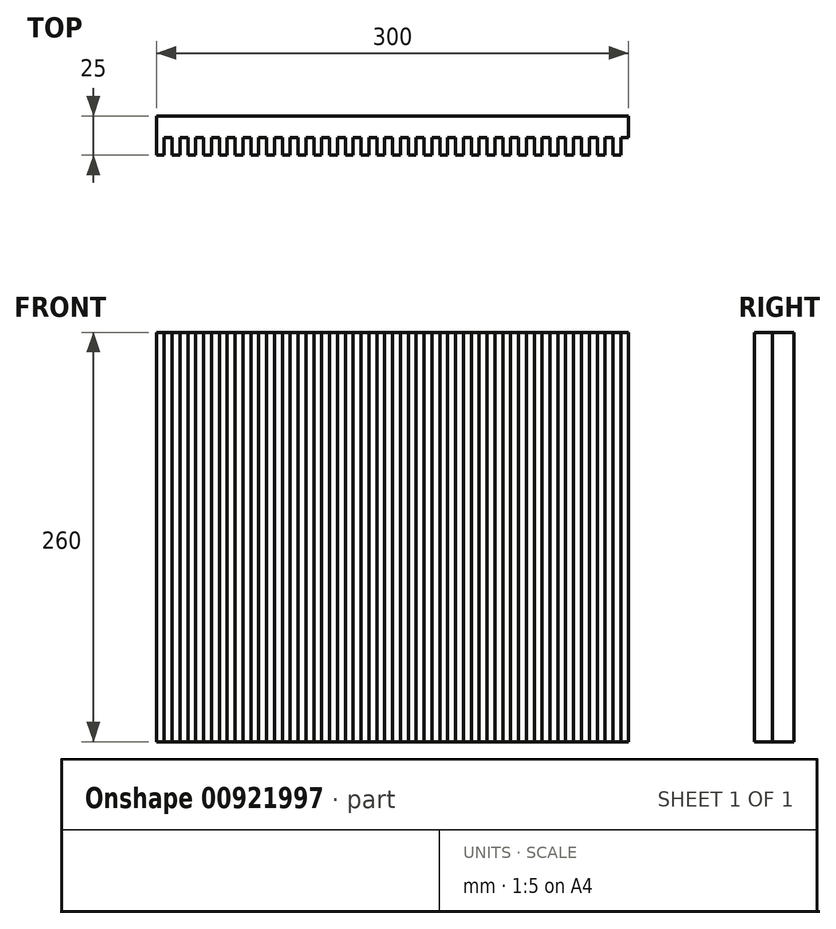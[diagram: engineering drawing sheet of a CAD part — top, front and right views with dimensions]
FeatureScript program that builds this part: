
annotation { "Feature Type Name" : "Feature", "Feature Type Description" : "" }
export const myFeature = defineFeature(function(context is Context, id is Id, definition is map)
    precondition{}
    {
        {
            var Q0;
            Q0=qCreatedBy(makeId("Front.planeOp"),FACE);
            var sketch = newSketch(context, id + "F0", { "sketchPlane" : qUnion([Q0])});
            skLineSegment(sketch, "E0.bottom", {"start": v(0, 0) * mm, "end": v(300, 0) * mm});
            skLineSegment(sketch, "E0.top", {"start": v(0, 260) * mm, "end": v(300, 260) * mm});
            skLineSegment(sketch, "E0.left", {"start": v(0, 0) * mm, "end": v(0, 260) * mm});
            skLineSegment(sketch, "E0.right", {"start": v(300, 0) * mm, "end": v(300, 260) * mm});
            skSolve(sketch);
        }
        {
            var Q0;
            Q0=makeQuery(id+"F0.imprint","IMPRINT",FACE,{"disambiguationData":[TD([[makeQuery(id+"F0.imprint","IMPRINT",EDGE,{"derivedFrom":sQuery(id+"F0.wireOp",EDGE,"E0.bottom")}),1.0]])]});
            extrude(context, id + "F1", {"entities" : qUnion([Q0]), "oppositeDirection" : true, "depth" : 25 * mm, "offsetDistance" : 25 * mm});
        }
        {
            var Q0;
            Q0=makeQuery(id+"F1.opExtrude","CAP_FACE",FACE,{"disambiguationData":[OSD([sQuery(id+"F0.wireOp",EDGE,"E0.bottom"),sQuery(id+"F0.wireOp",EDGE,"E0.top"),sQuery(id+"F0.wireOp",EDGE,"E0.left"),sQuery(id+"F0.wireOp",EDGE,"E0.right")])],"isStart":true});
            var sketch = newSketch(context, id + "F2", { "sketchPlane" : qUnion([Q0])});
            skLineSegment(sketch, "E1.bottom", {"start": v(5, 260) * mm, "end": v(10, 260) * mm});
            skLineSegment(sketch, "E1.top", {"start": v(5, 0) * mm, "end": v(10, 0) * mm});
            skLineSegment(sketch, "E1.left", {"start": v(5, 260) * mm, "end": v(5, 0) * mm});
            skLineSegment(sketch, "E1.right", {"start": v(10, 260) * mm, "end": v(10, 0) * mm});
            skLineSegment(sketch, "E2.1.0.0", {"start": v(15, 260) * mm, "end": v(15, 0) * mm});
            skLineSegment(sketch, "E2.1.0.1", {"start": v(20, 260) * mm, "end": v(20, 0) * mm});
            skLineSegment(sketch, "E2.1.0.2", {"start": v(15, 0) * mm, "end": v(20, 0) * mm});
            skLineSegment(sketch, "E2.1.0.3", {"start": v(15, 260) * mm, "end": v(20, 260) * mm});
            skLineSegment(sketch, "E2.2.0.0", {"start": v(25, 260) * mm, "end": v(25, 0) * mm});
            skLineSegment(sketch, "E2.2.0.1", {"start": v(30, 260) * mm, "end": v(30, 0) * mm});
            skLineSegment(sketch, "E2.2.0.2", {"start": v(25, 0) * mm, "end": v(30, 0) * mm});
            skLineSegment(sketch, "E2.2.0.3", {"start": v(25, 260) * mm, "end": v(30, 260) * mm});
            skLineSegment(sketch, "E2.3.0.0", {"start": v(35, 260) * mm, "end": v(35, 0) * mm});
            skLineSegment(sketch, "E2.3.0.1", {"start": v(40, 260) * mm, "end": v(40, 0) * mm});
            skLineSegment(sketch, "E2.3.0.2", {"start": v(35, 0) * mm, "end": v(40, 0) * mm});
            skLineSegment(sketch, "E2.3.0.3", {"start": v(35, 260) * mm, "end": v(40, 260) * mm});
            skLineSegment(sketch, "E2.4.0.0", {"start": v(45, 260) * mm, "end": v(45, 0) * mm});
            skLineSegment(sketch, "E2.4.0.1", {"start": v(50, 260) * mm, "end": v(50, 0) * mm});
            skLineSegment(sketch, "E2.4.0.2", {"start": v(45, 0) * mm, "end": v(50, 0) * mm});
            skLineSegment(sketch, "E2.4.0.3", {"start": v(45, 260) * mm, "end": v(50, 260) * mm});
            skLineSegment(sketch, "E2.5.0.0", {"start": v(55, 260) * mm, "end": v(55, 0) * mm});
            skLineSegment(sketch, "E2.5.0.1", {"start": v(60, 260) * mm, "end": v(60, 0) * mm});
            skLineSegment(sketch, "E2.5.0.2", {"start": v(55, 0) * mm, "end": v(60, 0) * mm});
            skLineSegment(sketch, "E2.5.0.3", {"start": v(55, 260) * mm, "end": v(60, 260) * mm});
            skLineSegment(sketch, "E2.6.0.0", {"start": v(65, 260) * mm, "end": v(65, 0) * mm});
            skLineSegment(sketch, "E2.6.0.1", {"start": v(70, 260) * mm, "end": v(70, 0) * mm});
            skLineSegment(sketch, "E2.6.0.2", {"start": v(65, 0) * mm, "end": v(70, 0) * mm});
            skLineSegment(sketch, "E2.6.0.3", {"start": v(65, 260) * mm, "end": v(70, 260) * mm});
            skLineSegment(sketch, "E2.7.0.0", {"start": v(75, 260) * mm, "end": v(75, 0) * mm});
            skLineSegment(sketch, "E2.7.0.1", {"start": v(80, 260) * mm, "end": v(80, 0) * mm});
            skLineSegment(sketch, "E2.7.0.2", {"start": v(75, 0) * mm, "end": v(80, 0) * mm});
            skLineSegment(sketch, "E2.7.0.3", {"start": v(75, 260) * mm, "end": v(80, 260) * mm});
            skLineSegment(sketch, "E2.8.0.0", {"start": v(85, 260) * mm, "end": v(85, 0) * mm});
            skLineSegment(sketch, "E2.8.0.1", {"start": v(90, 260) * mm, "end": v(90, 0) * mm});
            skLineSegment(sketch, "E2.8.0.2", {"start": v(85, 0) * mm, "end": v(90, 0) * mm});
            skLineSegment(sketch, "E2.8.0.3", {"start": v(85, 260) * mm, "end": v(90, 260) * mm});
            skLineSegment(sketch, "E2.9.0.0", {"start": v(95, 260) * mm, "end": v(95, 0) * mm});
            skLineSegment(sketch, "E2.9.0.1", {"start": v(100, 260) * mm, "end": v(100, 0) * mm});
            skLineSegment(sketch, "E2.9.0.2", {"start": v(95, 0) * mm, "end": v(100, 0) * mm});
            skLineSegment(sketch, "E2.9.0.3", {"start": v(95, 260) * mm, "end": v(100, 260) * mm});
            skLineSegment(sketch, "E2.10.0.0", {"start": v(105, 260) * mm, "end": v(105, 0) * mm});
            skLineSegment(sketch, "E2.10.0.1", {"start": v(110, 260) * mm, "end": v(110, 0) * mm});
            skLineSegment(sketch, "E2.10.0.2", {"start": v(105, 0) * mm, "end": v(110, 0) * mm});
            skLineSegment(sketch, "E2.10.0.3", {"start": v(105, 260) * mm, "end": v(110, 260) * mm});
            skLineSegment(sketch, "E2.11.0.0", {"start": v(115, 260) * mm, "end": v(115, 0) * mm});
            skLineSegment(sketch, "E2.11.0.1", {"start": v(120, 260) * mm, "end": v(120, 0) * mm});
            skLineSegment(sketch, "E2.11.0.2", {"start": v(115, 0) * mm, "end": v(120, 0) * mm});
            skLineSegment(sketch, "E2.11.0.3", {"start": v(115, 260) * mm, "end": v(120, 260) * mm});
            skLineSegment(sketch, "E2.12.0.0", {"start": v(125, 260) * mm, "end": v(125, 0) * mm});
            skLineSegment(sketch, "E2.12.0.1", {"start": v(130, 260) * mm, "end": v(130, 0) * mm});
            skLineSegment(sketch, "E2.12.0.2", {"start": v(125, 0) * mm, "end": v(130, 0) * mm});
            skLineSegment(sketch, "E2.12.0.3", {"start": v(125, 260) * mm, "end": v(130, 260) * mm});
            skLineSegment(sketch, "E2.13.0.0", {"start": v(135, 260) * mm, "end": v(135, 0) * mm});
            skLineSegment(sketch, "E2.13.0.1", {"start": v(140, 260) * mm, "end": v(140, 0) * mm});
            skLineSegment(sketch, "E2.13.0.2", {"start": v(135, 0) * mm, "end": v(140, 0) * mm});
            skLineSegment(sketch, "E2.13.0.3", {"start": v(135, 260) * mm, "end": v(140, 260) * mm});
            skLineSegment(sketch, "E2.14.0.0", {"start": v(145, 260) * mm, "end": v(145, 0) * mm});
            skLineSegment(sketch, "E2.14.0.1", {"start": v(150, 260) * mm, "end": v(150, 0) * mm});
            skLineSegment(sketch, "E2.14.0.2", {"start": v(145, 0) * mm, "end": v(150, 0) * mm});
            skLineSegment(sketch, "E2.14.0.3", {"start": v(145, 260) * mm, "end": v(150, 260) * mm});
            skLineSegment(sketch, "E2.15.0.0", {"start": v(155, 260) * mm, "end": v(155, 0) * mm});
            skLineSegment(sketch, "E2.15.0.1", {"start": v(160, 260) * mm, "end": v(160, 0) * mm});
            skLineSegment(sketch, "E2.15.0.2", {"start": v(155, 0) * mm, "end": v(160, 0) * mm});
            skLineSegment(sketch, "E2.15.0.3", {"start": v(155, 260) * mm, "end": v(160, 260) * mm});
            skLineSegment(sketch, "E2.16.0.0", {"start": v(165, 260) * mm, "end": v(165, 0) * mm});
            skLineSegment(sketch, "E2.16.0.1", {"start": v(170, 260) * mm, "end": v(170, 0) * mm});
            skLineSegment(sketch, "E2.16.0.2", {"start": v(165, 0) * mm, "end": v(170, 0) * mm});
            skLineSegment(sketch, "E2.16.0.3", {"start": v(165, 260) * mm, "end": v(170, 260) * mm});
            skLineSegment(sketch, "E2.17.0.0", {"start": v(175, 260) * mm, "end": v(175, 0) * mm});
            skLineSegment(sketch, "E2.17.0.1", {"start": v(180, 260) * mm, "end": v(180, 0) * mm});
            skLineSegment(sketch, "E2.17.0.2", {"start": v(175, 0) * mm, "end": v(180, 0) * mm});
            skLineSegment(sketch, "E2.17.0.3", {"start": v(175, 260) * mm, "end": v(180, 260) * mm});
            skLineSegment(sketch, "E2.18.0.0", {"start": v(185, 260) * mm, "end": v(185, 0) * mm});
            skLineSegment(sketch, "E2.18.0.1", {"start": v(190, 260) * mm, "end": v(190, 0) * mm});
            skLineSegment(sketch, "E2.18.0.2", {"start": v(185, 0) * mm, "end": v(190, 0) * mm});
            skLineSegment(sketch, "E2.18.0.3", {"start": v(185, 260) * mm, "end": v(190, 260) * mm});
            skLineSegment(sketch, "E2.19.0.0", {"start": v(195, 260) * mm, "end": v(195, 0) * mm});
            skLineSegment(sketch, "E2.19.0.1", {"start": v(200, 260) * mm, "end": v(200, 0) * mm});
            skLineSegment(sketch, "E2.19.0.2", {"start": v(195, 0) * mm, "end": v(200, 0) * mm});
            skLineSegment(sketch, "E2.19.0.3", {"start": v(195, 260) * mm, "end": v(200, 260) * mm});
            skLineSegment(sketch, "E2.20.0.0", {"start": v(205, 260) * mm, "end": v(205, 0) * mm});
            skLineSegment(sketch, "E2.20.0.1", {"start": v(210, 260) * mm, "end": v(210, 0) * mm});
            skLineSegment(sketch, "E2.20.0.2", {"start": v(205, 0) * mm, "end": v(210, 0) * mm});
            skLineSegment(sketch, "E2.20.0.3", {"start": v(205, 260) * mm, "end": v(210, 260) * mm});
            skLineSegment(sketch, "E2.21.0.0", {"start": v(215, 260) * mm, "end": v(215, 0) * mm});
            skLineSegment(sketch, "E2.21.0.1", {"start": v(220, 260) * mm, "end": v(220, 0) * mm});
            skLineSegment(sketch, "E2.21.0.2", {"start": v(215, 0) * mm, "end": v(220, 0) * mm});
            skLineSegment(sketch, "E2.21.0.3", {"start": v(215, 260) * mm, "end": v(220, 260) * mm});
            skLineSegment(sketch, "E2.22.0.0", {"start": v(225, 260) * mm, "end": v(225, 0) * mm});
            skLineSegment(sketch, "E2.22.0.1", {"start": v(230, 260) * mm, "end": v(230, 0) * mm});
            skLineSegment(sketch, "E2.22.0.2", {"start": v(225, 0) * mm, "end": v(230, 0) * mm});
            skLineSegment(sketch, "E2.22.0.3", {"start": v(225, 260) * mm, "end": v(230, 260) * mm});
            skLineSegment(sketch, "E2.23.0.0", {"start": v(235, 260) * mm, "end": v(235, 0) * mm});
            skLineSegment(sketch, "E2.23.0.1", {"start": v(240, 260) * mm, "end": v(240, 0) * mm});
            skLineSegment(sketch, "E2.23.0.2", {"start": v(235, 0) * mm, "end": v(240, 0) * mm});
            skLineSegment(sketch, "E2.23.0.3", {"start": v(235, 260) * mm, "end": v(240, 260) * mm});
            skLineSegment(sketch, "E2.24.0.0", {"start": v(245, 260) * mm, "end": v(245, 0) * mm});
            skLineSegment(sketch, "E2.24.0.1", {"start": v(250, 260) * mm, "end": v(250, 0) * mm});
            skLineSegment(sketch, "E2.24.0.2", {"start": v(245, 0) * mm, "end": v(250, 0) * mm});
            skLineSegment(sketch, "E2.24.0.3", {"start": v(245, 260) * mm, "end": v(250, 260) * mm});
            skLineSegment(sketch, "E2.25.0.0", {"start": v(255, 260) * mm, "end": v(255, 0) * mm});
            skLineSegment(sketch, "E2.25.0.1", {"start": v(260, 260) * mm, "end": v(260, 0) * mm});
            skLineSegment(sketch, "E2.25.0.2", {"start": v(255, 0) * mm, "end": v(260, 0) * mm});
            skLineSegment(sketch, "E2.25.0.3", {"start": v(255, 260) * mm, "end": v(260, 260) * mm});
            skLineSegment(sketch, "E2.26.0.0", {"start": v(265, 260) * mm, "end": v(265, 0) * mm});
            skLineSegment(sketch, "E2.26.0.1", {"start": v(270, 260) * mm, "end": v(270, 0) * mm});
            skLineSegment(sketch, "E2.26.0.2", {"start": v(265, 0) * mm, "end": v(270, 0) * mm});
            skLineSegment(sketch, "E2.26.0.3", {"start": v(265, 260) * mm, "end": v(270, 260) * mm});
            skLineSegment(sketch, "E2.27.0.0", {"start": v(275, 260) * mm, "end": v(275, 0) * mm});
            skLineSegment(sketch, "E2.27.0.1", {"start": v(280, 260) * mm, "end": v(280, 0) * mm});
            skLineSegment(sketch, "E2.27.0.2", {"start": v(275, 0) * mm, "end": v(280, 0) * mm});
            skLineSegment(sketch, "E2.27.0.3", {"start": v(275, 260) * mm, "end": v(280, 260) * mm});
            skLineSegment(sketch, "E2.28.0.0", {"start": v(285, 260) * mm, "end": v(285, 0) * mm});
            skLineSegment(sketch, "E2.28.0.1", {"start": v(290, 260) * mm, "end": v(290, 0) * mm});
            skLineSegment(sketch, "E2.28.0.2", {"start": v(285, 0) * mm, "end": v(290, 0) * mm});
            skLineSegment(sketch, "E2.28.0.3", {"start": v(285, 260) * mm, "end": v(290, 260) * mm});
            skLineSegment(sketch, "E2.29.0.0", {"start": v(295, 260) * mm, "end": v(295, 0) * mm});
            skLineSegment(sketch, "E2.29.0.1", {"start": v(300, 260) * mm, "end": v(300, 0) * mm});
            skLineSegment(sketch, "E2.29.0.2", {"start": v(295, 0) * mm, "end": v(300, 0) * mm});
            skLineSegment(sketch, "E2.29.0.3", {"start": v(295, 260) * mm, "end": v(300, 260) * mm});
            skLineSegment(sketch, "E2.30.0.0", {"start": v(305, 260) * mm, "end": v(305, 0) * mm});
            skLineSegment(sketch, "E2.30.0.1", {"start": v(310, 260) * mm, "end": v(310, 0) * mm});
            skLineSegment(sketch, "E2.30.0.2", {"start": v(305, 0) * mm, "end": v(310, 0) * mm});
            skLineSegment(sketch, "E2.30.0.3", {"start": v(305, 260) * mm, "end": v(310, 260) * mm});
            skLineSegment(sketch, "E2.31.0.0", {"start": v(315, 260) * mm, "end": v(315, 0) * mm});
            skLineSegment(sketch, "E2.31.0.1", {"start": v(320, 260) * mm, "end": v(320, 0) * mm});
            skLineSegment(sketch, "E2.31.0.2", {"start": v(315, 0) * mm, "end": v(320, 0) * mm});
            skLineSegment(sketch, "E2.31.0.3", {"start": v(315, 260) * mm, "end": v(320, 260) * mm});
            skLineSegment(sketch, "E2.32.0.0", {"start": v(325, 260) * mm, "end": v(325, 0) * mm});
            skLineSegment(sketch, "E2.32.0.1", {"start": v(330, 260) * mm, "end": v(330, 0) * mm});
            skLineSegment(sketch, "E2.32.0.2", {"start": v(325, 0) * mm, "end": v(330, 0) * mm});
            skLineSegment(sketch, "E2.32.0.3", {"start": v(325, 260) * mm, "end": v(330, 260) * mm});
            skLineSegment(sketch, "E2.33.0.0", {"start": v(335, 260) * mm, "end": v(335, 0) * mm});
            skLineSegment(sketch, "E2.33.0.1", {"start": v(340, 260) * mm, "end": v(340, 0) * mm});
            skLineSegment(sketch, "E2.33.0.2", {"start": v(335, 0) * mm, "end": v(340, 0) * mm});
            skLineSegment(sketch, "E2.33.0.3", {"start": v(335, 260) * mm, "end": v(340, 260) * mm});
            skLineSegment(sketch, "E2.34.0.0", {"start": v(345, 260) * mm, "end": v(345, 0) * mm});
            skLineSegment(sketch, "E2.34.0.1", {"start": v(350, 260) * mm, "end": v(350, 0) * mm});
            skLineSegment(sketch, "E2.34.0.2", {"start": v(345, 0) * mm, "end": v(350, 0) * mm});
            skLineSegment(sketch, "E2.34.0.3", {"start": v(345, 260) * mm, "end": v(350, 260) * mm});
            skLineSegment(sketch, "E2.35.0.0", {"start": v(355, 260) * mm, "end": v(355, 0) * mm});
            skLineSegment(sketch, "E2.35.0.1", {"start": v(360, 260) * mm, "end": v(360, 0) * mm});
            skLineSegment(sketch, "E2.35.0.2", {"start": v(355, 0) * mm, "end": v(360, 0) * mm});
            skLineSegment(sketch, "E2.35.0.3", {"start": v(355, 260) * mm, "end": v(360, 260) * mm});
            skLineSegment(sketch, "E2.36.0.0", {"start": v(365, 260) * mm, "end": v(365, 0) * mm});
            skLineSegment(sketch, "E2.36.0.1", {"start": v(370, 260) * mm, "end": v(370, 0) * mm});
            skLineSegment(sketch, "E2.36.0.2", {"start": v(365, 0) * mm, "end": v(370, 0) * mm});
            skLineSegment(sketch, "E2.36.0.3", {"start": v(365, 260) * mm, "end": v(370, 260) * mm});
            skLineSegment(sketch, "E2.37.0.0", {"start": v(375, 260) * mm, "end": v(375, 0) * mm});
            skLineSegment(sketch, "E2.37.0.1", {"start": v(380, 260) * mm, "end": v(380, 0) * mm});
            skLineSegment(sketch, "E2.37.0.2", {"start": v(375, 0) * mm, "end": v(380, 0) * mm});
            skLineSegment(sketch, "E2.37.0.3", {"start": v(375, 260) * mm, "end": v(380, 260) * mm});
            skLineSegment(sketch, "E2.38.0.0", {"start": v(385, 260) * mm, "end": v(385, 0) * mm});
            skLineSegment(sketch, "E2.38.0.1", {"start": v(390, 260) * mm, "end": v(390, 0) * mm});
            skLineSegment(sketch, "E2.38.0.2", {"start": v(385, 0) * mm, "end": v(390, 0) * mm});
            skLineSegment(sketch, "E2.38.0.3", {"start": v(385, 260) * mm, "end": v(390, 260) * mm});
            skLineSegment(sketch, "E2.39.0.0", {"start": v(395, 260) * mm, "end": v(395, 0) * mm});
            skLineSegment(sketch, "E2.39.0.1", {"start": v(400, 260) * mm, "end": v(400, 0) * mm});
            skLineSegment(sketch, "E2.39.0.2", {"start": v(395, 0) * mm, "end": v(400, 0) * mm});
            skLineSegment(sketch, "E2.39.0.3", {"start": v(395, 260) * mm, "end": v(400, 260) * mm});
            skLineSegment(sketch, "E2.direction1", {"start": v(5, 0) * mm, "end": v(15, 0) * mm, "construction": true});
            skLineSegment(sketch, "E3.0.40.0", {"start": v(405, 260) * mm, "end": v(405, 0) * mm});
            skLineSegment(sketch, "E3.3.40.0", {"start": v(410, 260) * mm, "end": v(410, 0) * mm});
            skLineSegment(sketch, "E3.6.40.0", {"start": v(405, 0) * mm, "end": v(410, 0) * mm});
            skLineSegment(sketch, "E3.9.40.0", {"start": v(405, 260) * mm, "end": v(410, 260) * mm});
            skLineSegment(sketch, "E3.0.41.0", {"start": v(415, 260) * mm, "end": v(415, 0) * mm});
            skLineSegment(sketch, "E3.3.41.0", {"start": v(420, 260) * mm, "end": v(420, 0) * mm});
            skLineSegment(sketch, "E3.6.41.0", {"start": v(415, 0) * mm, "end": v(420, 0) * mm});
            skLineSegment(sketch, "E3.9.41.0", {"start": v(415, 260) * mm, "end": v(420, 260) * mm});
            skLineSegment(sketch, "E3.0.42.0", {"start": v(425, 260) * mm, "end": v(425, 0) * mm});
            skLineSegment(sketch, "E3.3.42.0", {"start": v(430, 260) * mm, "end": v(430, 0) * mm});
            skLineSegment(sketch, "E3.6.42.0", {"start": v(425, 0) * mm, "end": v(430, 0) * mm});
            skLineSegment(sketch, "E3.9.42.0", {"start": v(425, 260) * mm, "end": v(430, 260) * mm});
            skLineSegment(sketch, "E3.0.43.0", {"start": v(435, 260) * mm, "end": v(435, 0) * mm});
            skLineSegment(sketch, "E3.3.43.0", {"start": v(440, 260) * mm, "end": v(440, 0) * mm});
            skLineSegment(sketch, "E3.6.43.0", {"start": v(435, 0) * mm, "end": v(440, 0) * mm});
            skLineSegment(sketch, "E3.9.43.0", {"start": v(435, 260) * mm, "end": v(440, 260) * mm});
            skLineSegment(sketch, "E3.0.44.0", {"start": v(445, 260) * mm, "end": v(445, 0) * mm});
            skLineSegment(sketch, "E3.3.44.0", {"start": v(450, 260) * mm, "end": v(450, 0) * mm});
            skLineSegment(sketch, "E3.6.44.0", {"start": v(445, 0) * mm, "end": v(450, 0) * mm});
            skLineSegment(sketch, "E3.9.44.0", {"start": v(445, 260) * mm, "end": v(450, 260) * mm});
            skLineSegment(sketch, "E3.0.45.0", {"start": v(455, 260) * mm, "end": v(455, 0) * mm});
            skLineSegment(sketch, "E3.3.45.0", {"start": v(460, 260) * mm, "end": v(460, 0) * mm});
            skLineSegment(sketch, "E3.6.45.0", {"start": v(455, 0) * mm, "end": v(460, 0) * mm});
            skLineSegment(sketch, "E3.9.45.0", {"start": v(455, 260) * mm, "end": v(460, 260) * mm});
            skLineSegment(sketch, "E3.0.46.0", {"start": v(465, 260) * mm, "end": v(465, 0) * mm});
            skLineSegment(sketch, "E3.3.46.0", {"start": v(470, 260) * mm, "end": v(470, 0) * mm});
            skLineSegment(sketch, "E3.6.46.0", {"start": v(465, 0) * mm, "end": v(470, 0) * mm});
            skLineSegment(sketch, "E3.9.46.0", {"start": v(465, 260) * mm, "end": v(470, 260) * mm});
            skLineSegment(sketch, "E3.0.47.0", {"start": v(475, 260) * mm, "end": v(475, 0) * mm});
            skLineSegment(sketch, "E3.3.47.0", {"start": v(480, 260) * mm, "end": v(480, 0) * mm});
            skLineSegment(sketch, "E3.6.47.0", {"start": v(475, 0) * mm, "end": v(480, 0) * mm});
            skLineSegment(sketch, "E3.9.47.0", {"start": v(475, 260) * mm, "end": v(480, 260) * mm});
            skLineSegment(sketch, "E3.0.48.0", {"start": v(485, 260) * mm, "end": v(485, 0) * mm});
            skLineSegment(sketch, "E3.3.48.0", {"start": v(490, 260) * mm, "end": v(490, 0) * mm});
            skLineSegment(sketch, "E3.6.48.0", {"start": v(485, 0) * mm, "end": v(490, 0) * mm});
            skLineSegment(sketch, "E3.9.48.0", {"start": v(485, 260) * mm, "end": v(490, 260) * mm});
            skLineSegment(sketch, "E3.0.49.0", {"start": v(495, 260) * mm, "end": v(495, 0) * mm});
            skLineSegment(sketch, "E3.3.49.0", {"start": v(500, 260) * mm, "end": v(500, 0) * mm});
            skLineSegment(sketch, "E3.6.49.0", {"start": v(495, 0) * mm, "end": v(500, 0) * mm});
            skLineSegment(sketch, "E3.9.49.0", {"start": v(495, 260) * mm, "end": v(500, 260) * mm});
            skSolve(sketch);
        }
        {
            var Q0;
            Q0 = qSketchRegion(id + "F2", true);
            extrude(context, id + "F3", {"entities" : qUnion([Q0]), "operationType" : NewBodyOperationType.REMOVE, "oppositeDirection" : true, "depth" : 11.2 * mm, "offsetDistance" : 25 * mm});
        }
    });
